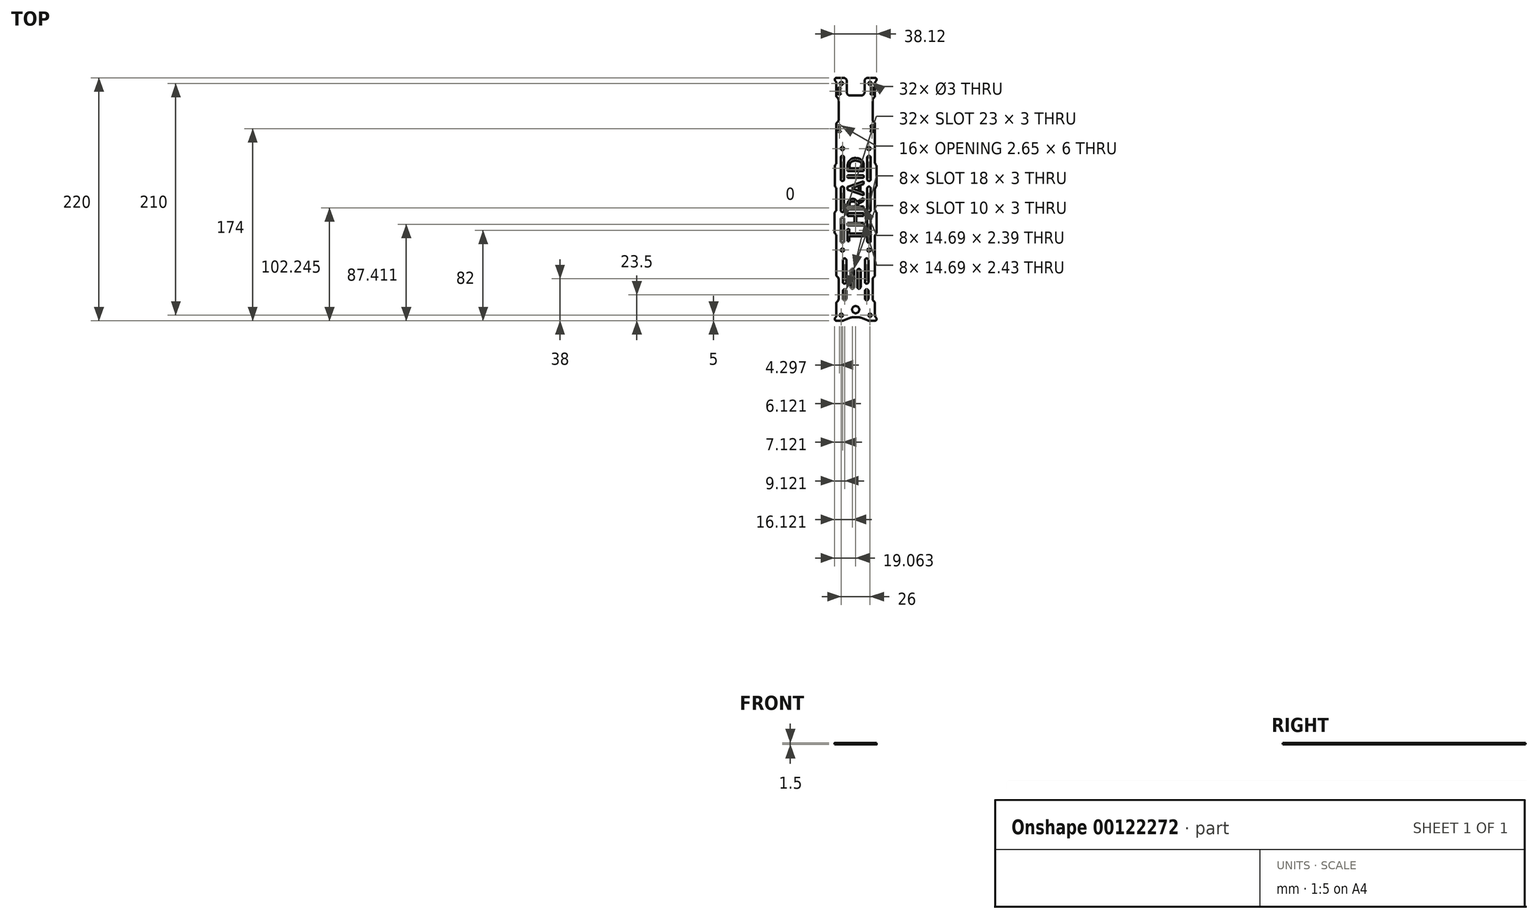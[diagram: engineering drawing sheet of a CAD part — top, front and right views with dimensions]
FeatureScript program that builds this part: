
annotation { "Feature Type Name" : "Feature", "Feature Type Description" : "" }
export const myFeature = defineFeature(function(context is Context, id is Id, definition is map)
    precondition{}
    {
        {
            var Q0;
            Q0=qCreatedBy(makeId("Top.planeOp"),FACE);
            var sketch = newSketch(context, id + "F0", { "sketchPlane" : qUnion([Q0])});
            skArc(sketch, "E0", {"start": v(-17.44, 110) * mm, "mid": v(-18.84, 109.04) * mm, "end": v(-18.44, 107.38) * mm});
            skArc(sketch, "E1", {"start": v(18.56, 107.38) * mm, "mid": v(18.96, 109.04) * mm, "end": v(17.56, 110) * mm});
            skArc(sketch, "E2", {"start": v(-17.44, 105.15) * mm, "mid": v(-17.7, 106.37) * mm, "end": v(-18.44, 107.38) * mm});
            skArc(sketch, "E3", {"start": v(18.56, 107.38) * mm, "mid": v(17.82, 106.37) * mm, "end": v(17.56, 105.15) * mm});
            skLineSegment(sketch, "E4", {"start": v(-17.44, -110) * mm, "end": v(-12.02, -110) * mm});
            skLineSegment(sketch, "E5", {"start": v(12.14, -110) * mm, "end": v(17.56, -110) * mm});
            skArc(sketch, "E6", {"start": v(-18.44, -107.38) * mm, "mid": v(-18.84, -109.04) * mm, "end": v(-17.44, -110) * mm});
            skArc(sketch, "E7", {"start": v(17.56, -110) * mm, "mid": v(18.96, -109.04) * mm, "end": v(18.56, -107.38) * mm});
            skLineSegment(sketch, "E8", {"start": v(11.03, -109.79) * mm, "end": v(4.6, -107.21) * mm});
            skLineSegment(sketch, "E9", {"start": v(-4.47, -107.21) * mm, "end": v(-10.9, -109.79) * mm});
            skArc(sketch, "E10", {"start": v(-18.44, -107.38) * mm, "mid": v(-17.7, -106.37) * mm, "end": v(-17.44, -105.15) * mm});
            skArc(sketch, "E11", {"start": v(-12.02, -110) * mm, "mid": v(-11.45, -109.95) * mm, "end": v(-10.9, -109.79) * mm});
            skArc(sketch, "E12", {"start": v(-3.36, -107) * mm, "mid": v(-3.93, -107.05) * mm, "end": v(-4.47, -107.21) * mm});
            skArc(sketch, "E13", {"start": v(4.6, -107.21) * mm, "mid": v(4.05, -107.05) * mm, "end": v(3.48, -107) * mm});
            skArc(sketch, "E14", {"start": v(11.03, -109.79) * mm, "mid": v(11.57, -109.95) * mm, "end": v(12.14, -110) * mm});
            skArc(sketch, "E15", {"start": v(17.56, -105.15) * mm, "mid": v(17.82, -106.37) * mm, "end": v(18.56, -107.38) * mm});
            skCircle(sketch, "E16", {"center": v(12.06, -46) * mm, "radius": 1.5 * mm});
            skCircle(sketch, "E17", {"center": v(-11.94, -46) * mm, "radius": 1.5 * mm});
            skLineSegment(sketch, "E18", {"start": v(15.56, 77.5) * mm, "end": v(15.56, 84.5) * mm});
            skLineSegment(sketch, "E19", {"start": v(-15.44, 84.5) * mm, "end": v(-15.44, 77.5) * mm});
            skLineSegment(sketch, "E20", {"start": v(15.56, 90.17) * mm, "end": v(15.56, 71.83) * mm});
            skLineSegment(sketch, "E21", {"start": v(17.56, 105.15) * mm, "end": v(17.56, 93.83) * mm});
            skLineSegment(sketch, "E22", {"start": v(17.56, 68.17) * mm, "end": v(17.56, 45.82) * mm});
            skLineSegment(sketch, "E23", {"start": v(16.15, 91.59) * mm, "end": v(16.98, 92.41) * mm});
            skLineSegment(sketch, "E24", {"start": v(16.98, 69.59) * mm, "end": v(16.15, 70.41) * mm});
            skLineSegment(sketch, "E25", {"start": v(-15.44, 71.83) * mm, "end": v(-15.44, 90.17) * mm});
            skLineSegment(sketch, "E26", {"start": v(-16.02, 91.59) * mm, "end": v(-16.85, 92.41) * mm});
            skLineSegment(sketch, "E27", {"start": v(-16.85, 69.59) * mm, "end": v(-16.02, 70.41) * mm});
            skLineSegment(sketch, "E28", {"start": v(-17.44, 105.15) * mm, "end": v(-17.44, 93.83) * mm});
            skLineSegment(sketch, "E29", {"start": v(-17.44, 45.82) * mm, "end": v(-17.44, 68.17) * mm});
            skArc(sketch, "E30", {"start": v(-17.44, 93.83) * mm, "mid": v(-17.29, 93.06) * mm, "end": v(-16.85, 92.41) * mm});
            skArc(sketch, "E31", {"start": v(-15.44, 90.17) * mm, "mid": v(-15.6, 90.94) * mm, "end": v(-16.02, 91.59) * mm});
            skArc(sketch, "E32", {"start": v(-16.85, 69.59) * mm, "mid": v(-17.29, 68.94) * mm, "end": v(-17.44, 68.17) * mm});
            skArc(sketch, "E33", {"start": v(-16.02, 70.41) * mm, "mid": v(-15.6, 71.06) * mm, "end": v(-15.44, 71.83) * mm});
            skArc(sketch, "E34", {"start": v(16.98, 92.41) * mm, "mid": v(17.4, 93.06) * mm, "end": v(17.56, 93.83) * mm});
            skArc(sketch, "E35", {"start": v(16.15, 91.59) * mm, "mid": v(15.71, 90.94) * mm, "end": v(15.56, 90.17) * mm});
            skArc(sketch, "E36", {"start": v(15.56, 71.83) * mm, "mid": v(15.71, 71.06) * mm, "end": v(16.15, 70.41) * mm});
            skArc(sketch, "E37", {"start": v(17.56, 68.17) * mm, "mid": v(17.4, 68.94) * mm, "end": v(16.98, 69.59) * mm});
            skLineSegment(sketch, "E38", {"start": v(15.56, -91.32) * mm, "end": v(15.56, -72.15) * mm});
            skLineSegment(sketch, "E39", {"start": v(-17.44, -45.82) * mm, "end": v(-17.44, -68.49) * mm});
            skLineSegment(sketch, "E40", {"start": v(17.56, -68.49) * mm, "end": v(17.56, -45.82) * mm});
            skLineSegment(sketch, "E41", {"start": v(16.98, -69.9) * mm, "end": v(16.15, -70.73) * mm});
            skLineSegment(sketch, "E42", {"start": v(-16.02, -70.73) * mm, "end": v(-16.85, -69.9) * mm});
            skLineSegment(sketch, "E43", {"start": v(17.56, -93.32) * mm, "end": v(15.56, -91.32) * mm});
            skLineSegment(sketch, "E44", {"start": v(-16.85, -92.73) * mm, "end": v(-16.02, -91.9) * mm});
            skLineSegment(sketch, "E45", {"start": v(-17.44, -94.15) * mm, "end": v(-17.44, -105.15) * mm});
            skLineSegment(sketch, "E46", {"start": v(17.56, -105.15) * mm, "end": v(17.56, -93.32) * mm});
            skLineSegment(sketch, "E47", {"start": v(-15.44, -72.15) * mm, "end": v(-15.44, -90.49) * mm});
            skArc(sketch, "E48", {"start": v(-16.85, -92.73) * mm, "mid": v(-17.29, -93.38) * mm, "end": v(-17.44, -94.15) * mm});
            skArc(sketch, "E49", {"start": v(-16.02, -91.9) * mm, "mid": v(-15.6, -91.25) * mm, "end": v(-15.44, -90.49) * mm});
            skArc(sketch, "E50", {"start": v(-17.44, -68.49) * mm, "mid": v(-17.29, -69.25) * mm, "end": v(-16.85, -69.9) * mm});
            skArc(sketch, "E51", {"start": v(-15.44, -72.15) * mm, "mid": v(-15.6, -71.38) * mm, "end": v(-16.02, -70.73) * mm});
            skArc(sketch, "E52", {"start": v(16.15, -70.73) * mm, "mid": v(15.71, -71.38) * mm, "end": v(15.56, -72.15) * mm});
            skArc(sketch, "E53", {"start": v(16.98, -69.9) * mm, "mid": v(17.4, -69.25) * mm, "end": v(17.56, -68.49) * mm});
            skCircle(sketch, "E54", {"center": v(-11.94, 46) * mm, "radius": 1.5 * mm});
            skCircle(sketch, "E55", {"center": v(12.06, 46) * mm, "radius": 1.5 * mm});
            skLineSegment(sketch, "E56", {"start": v(3.48, -107) * mm, "end": v(-3.36, -107) * mm});
            skLineSegment(sketch, "E57", {"start": v(17.56, -9.4) * mm, "end": v(17.56, 9.33) * mm});
            skLineSegment(sketch, "E58", {"start": v(-17.44, 9.33) * mm, "end": v(-17.44, -9.3) * mm});
            skLineSegment(sketch, "E59", {"start": v(17.56, 45.82) * mm, "end": v(17.56, 33.17) * mm});
            skLineSegment(sketch, "E60", {"start": v(17.56, -33.14) * mm, "end": v(17.56, -45.82) * mm});
            skLineSegment(sketch, "E61", {"start": v(-17.44, -45.82) * mm, "end": v(-17.44, -33.23) * mm});
            skLineSegment(sketch, "E62", {"start": v(-17.44, 33.17) * mm, "end": v(-17.44, 45.82) * mm});
            skLineSegment(sketch, "E63", {"start": v(19.06, 12.67) * mm, "end": v(19.06, 29.83) * mm});
            skLineSegment(sketch, "E64", {"start": v(-18.94, 29.83) * mm, "end": v(-18.94, 12.67) * mm});
            skLineSegment(sketch, "E65", {"start": v(18.94, -29.92) * mm, "end": v(18.94, -12.66) * mm});
            skLineSegment(sketch, "E66", {"start": v(-19.06, -12.75) * mm, "end": v(-19.06, -29.83) * mm});
            skLineSegment(sketch, "E67", {"start": v(-17.9, -31.94) * mm, "end": v(-18.6, -31.11) * mm});
            skLineSegment(sketch, "E68", {"start": v(17.93, -31.98) * mm, "end": v(18.57, -31.08) * mm});
            skLineSegment(sketch, "E69", {"start": v(18.6, -11.55) * mm, "end": v(17.9, -10.5) * mm});
            skLineSegment(sketch, "E70", {"start": v(-18.63, -11.51) * mm, "end": v(-17.87, -10.54) * mm});
            skLineSegment(sketch, "E71", {"start": v(17.96, 10.53) * mm, "end": v(18.66, 11.47) * mm});
            skLineSegment(sketch, "E72", {"start": v(-17.84, 10.53) * mm, "end": v(-18.54, 11.47) * mm});
            skLineSegment(sketch, "E73", {"start": v(-18.54, 31.03) * mm, "end": v(-17.84, 31.97) * mm});
            skLineSegment(sketch, "E74", {"start": v(17.96, 31.97) * mm, "end": v(18.66, 31.03) * mm});
            skArc(sketch, "E75", {"start": v(-17.84, 31.97) * mm, "mid": v(-17.54, 32.53) * mm, "end": v(-17.44, 33.17) * mm});
            skArc(sketch, "E76", {"start": v(-18.54, 31.03) * mm, "mid": v(-18.84, 30.47) * mm, "end": v(-18.94, 29.83) * mm});
            skArc(sketch, "E77", {"start": v(-18.94, 12.67) * mm, "mid": v(-18.84, 12.03) * mm, "end": v(-18.54, 11.47) * mm});
            skArc(sketch, "E78", {"start": v(-17.44, 9.33) * mm, "mid": v(-17.54, 9.97) * mm, "end": v(-17.84, 10.53) * mm});
            skArc(sketch, "E79", {"start": v(17.56, 33.17) * mm, "mid": v(17.66, 32.53) * mm, "end": v(17.96, 31.97) * mm});
            skArc(sketch, "E80", {"start": v(19.06, 29.83) * mm, "mid": v(18.96, 30.47) * mm, "end": v(18.66, 31.03) * mm});
            skArc(sketch, "E81", {"start": v(18.66, 11.47) * mm, "mid": v(18.96, 12.03) * mm, "end": v(19.06, 12.67) * mm});
            skArc(sketch, "E82", {"start": v(17.96, 10.53) * mm, "mid": v(17.66, 9.97) * mm, "end": v(17.56, 9.33) * mm});
            skArc(sketch, "E83", {"start": v(17.56, -9.4) * mm, "mid": v(17.65, -9.97) * mm, "end": v(17.9, -10.5) * mm});
            skArc(sketch, "E84", {"start": v(18.94, -12.66) * mm, "mid": v(18.85, -12.08) * mm, "end": v(18.6, -11.55) * mm});
            skArc(sketch, "E85", {"start": v(-17.87, -10.54) * mm, "mid": v(-17.55, -9.96) * mm, "end": v(-17.44, -9.3) * mm});
            skArc(sketch, "E86", {"start": v(-18.63, -11.51) * mm, "mid": v(-18.95, -12.1) * mm, "end": v(-19.06, -12.75) * mm});
            skArc(sketch, "E87", {"start": v(18.57, -31.08) * mm, "mid": v(18.84, -30.53) * mm, "end": v(18.94, -29.92) * mm});
            skArc(sketch, "E88", {"start": v(17.93, -31.98) * mm, "mid": v(17.66, -32.53) * mm, "end": v(17.56, -33.14) * mm});
            skArc(sketch, "E89", {"start": v(-17.44, -33.23) * mm, "mid": v(-17.56, -32.54) * mm, "end": v(-17.9, -31.94) * mm});
            skArc(sketch, "E90", {"start": v(-19.06, -29.83) * mm, "mid": v(-18.94, -30.51) * mm, "end": v(-18.6, -31.11) * mm});
            skLineSegment(sketch, "E91", {"start": v(13.56, -10) * mm, "end": v(13.56, 10) * mm});
            skLineSegment(sketch, "E92", {"start": v(10.56, 10) * mm, "end": v(10.56, -10) * mm});
            skArc(sketch, "E93", {"start": v(13.56, 10) * mm, "mid": v(12.06, 11.5) * mm, "end": v(10.56, 10) * mm});
            skArc(sketch, "E94", {"start": v(10.56, -10) * mm, "mid": v(12.06, -11.5) * mm, "end": v(13.56, -10) * mm});
            skLineSegment(sketch, "E95", {"start": v(-10.44, -10) * mm, "end": v(-10.44, 10) * mm});
            skLineSegment(sketch, "E96", {"start": v(-13.44, 10) * mm, "end": v(-13.44, -10) * mm});
            skArc(sketch, "E97", {"start": v(-10.44, 10) * mm, "mid": v(-11.94, 11.5) * mm, "end": v(-13.44, 10) * mm});
            skArc(sketch, "E98", {"start": v(-13.44, -10) * mm, "mid": v(-11.94, -11.5) * mm, "end": v(-10.44, -10) * mm});
            skLineSegment(sketch, "E99", {"start": v(13.56, 18) * mm, "end": v(13.56, 38) * mm});
            skLineSegment(sketch, "E100", {"start": v(10.56, 38) * mm, "end": v(10.56, 18) * mm});
            skArc(sketch, "E101", {"start": v(13.56, 38) * mm, "mid": v(12.06, 39.5) * mm, "end": v(10.56, 38) * mm});
            skArc(sketch, "E102", {"start": v(10.56, 18) * mm, "mid": v(12.06, 16.5) * mm, "end": v(13.56, 18) * mm});
            skLineSegment(sketch, "E103", {"start": v(-10.44, 18) * mm, "end": v(-10.44, 38) * mm});
            skLineSegment(sketch, "E104", {"start": v(-13.44, 38) * mm, "end": v(-13.44, 18) * mm});
            skArc(sketch, "E105", {"start": v(-10.44, 38) * mm, "mid": v(-11.94, 39.5) * mm, "end": v(-13.44, 38) * mm});
            skArc(sketch, "E106", {"start": v(-13.44, 18) * mm, "mid": v(-11.94, 16.5) * mm, "end": v(-10.44, 18) * mm});
            skLineSegment(sketch, "E107", {"start": v(13.56, -38) * mm, "end": v(13.56, -18) * mm});
            skLineSegment(sketch, "E108", {"start": v(10.56, -18) * mm, "end": v(10.56, -38) * mm});
            skArc(sketch, "E109", {"start": v(13.56, -18) * mm, "mid": v(12.06, -16.5) * mm, "end": v(10.56, -18) * mm});
            skArc(sketch, "E110", {"start": v(10.56, -38) * mm, "mid": v(12.06, -39.5) * mm, "end": v(13.56, -38) * mm});
            skLineSegment(sketch, "E111", {"start": v(-10.44, -38) * mm, "end": v(-10.44, -18) * mm});
            skLineSegment(sketch, "E112", {"start": v(-13.44, -18) * mm, "end": v(-13.44, -38) * mm});
            skArc(sketch, "E113", {"start": v(-10.44, -18) * mm, "mid": v(-11.94, -16.5) * mm, "end": v(-13.44, -18) * mm});
            skArc(sketch, "E114", {"start": v(-13.44, -38) * mm, "mid": v(-11.94, -39.5) * mm, "end": v(-10.44, -38) * mm});
            skLineSegment(sketch, "E115", {"start": v(11.56, -75) * mm, "end": v(11.56, -55) * mm});
            skLineSegment(sketch, "E116", {"start": v(8.56, -55) * mm, "end": v(8.56, -75) * mm});
            skArc(sketch, "E117", {"start": v(11.56, -55) * mm, "mid": v(10.06, -53.5) * mm, "end": v(8.56, -55) * mm});
            skArc(sketch, "E118", {"start": v(8.56, -75) * mm, "mid": v(10.06, -76.5) * mm, "end": v(11.56, -75) * mm});
            skLineSegment(sketch, "E119", {"start": v(-8.44, -75) * mm, "end": v(-8.44, -55) * mm});
            skLineSegment(sketch, "E120", {"start": v(-11.44, -55) * mm, "end": v(-11.44, -75) * mm});
            skArc(sketch, "E121", {"start": v(-8.44, -55) * mm, "mid": v(-9.94, -53.5) * mm, "end": v(-11.44, -55) * mm});
            skArc(sketch, "E122", {"start": v(-11.44, -75) * mm, "mid": v(-9.94, -76.5) * mm, "end": v(-8.44, -75) * mm});
            skLineSegment(sketch, "E123", {"start": v(11.56, -90) * mm, "end": v(11.56, -83) * mm});
            skLineSegment(sketch, "E124", {"start": v(8.56, -83) * mm, "end": v(8.56, -90) * mm});
            skLineSegment(sketch, "E125", {"start": v(-8.44, -90) * mm, "end": v(-8.44, -83) * mm});
            skLineSegment(sketch, "E126", {"start": v(-11.44, -83) * mm, "end": v(-11.44, -90) * mm});
            skArc(sketch, "E127", {"start": v(-8.44, -83) * mm, "mid": v(-9.94, -81.5) * mm, "end": v(-11.44, -83) * mm});
            skArc(sketch, "E128", {"start": v(11.56, -83) * mm, "mid": v(10.06, -81.5) * mm, "end": v(8.56, -83) * mm});
            skLineSegment(sketch, "E129", {"start": v(-13.94, 101) * mm, "end": v(-15.59, 101) * mm});
            skLineSegment(sketch, "E130", {"start": v(-15.59, 61) * mm, "end": v(-13.94, 61) * mm});
            skLineSegment(sketch, "E131", {"start": v(-13.94, 67) * mm, "end": v(-15.59, 67) * mm});
            skLineSegment(sketch, "E132", {"start": v(14.06, 61) * mm, "end": v(15.71, 61) * mm});
            skLineSegment(sketch, "E133", {"start": v(15.71, 67) * mm, "end": v(14.06, 67) * mm});
            skLineSegment(sketch, "E134", {"start": v(15.71, 101) * mm, "end": v(14.06, 101) * mm});
            skLineSegment(sketch, "E135", {"start": v(-15.59, 95) * mm, "end": v(-13.94, 95) * mm});
            skLineSegment(sketch, "E136", {"start": v(14.06, 95) * mm, "end": v(15.71, 95) * mm});
            skArc(sketch, "E137", {"start": v(-15.59, 101) * mm, "mid": v(-16.07, 100.63) * mm, "end": v(-15.84, 100.07) * mm});
            skArc(sketch, "E138", {"start": v(-15.84, 95.93) * mm, "mid": v(-16.07, 95.37) * mm, "end": v(-15.59, 95) * mm});
            skArc(sketch, "E139", {"start": v(-13.94, 95) * mm, "mid": v(-13.46, 95.37) * mm, "end": v(-13.69, 95.93) * mm});
            skArc(sketch, "E140", {"start": v(-13.69, 100.07) * mm, "mid": v(-13.46, 100.63) * mm, "end": v(-13.94, 101) * mm});
            skArc(sketch, "E141", {"start": v(14.06, 101) * mm, "mid": v(13.58, 100.63) * mm, "end": v(13.81, 100.07) * mm});
            skArc(sketch, "E142", {"start": v(13.81, 95.93) * mm, "mid": v(13.58, 95.37) * mm, "end": v(14.06, 95) * mm});
            skArc(sketch, "E143", {"start": v(15.71, 95) * mm, "mid": v(16.2, 95.37) * mm, "end": v(15.96, 95.93) * mm});
            skArc(sketch, "E144", {"start": v(15.96, 100.07) * mm, "mid": v(16.2, 100.63) * mm, "end": v(15.71, 101) * mm});
            skArc(sketch, "E145", {"start": v(14.06, 67) * mm, "mid": v(13.58, 66.63) * mm, "end": v(13.81, 66.07) * mm});
            skArc(sketch, "E146", {"start": v(13.81, 61.93) * mm, "mid": v(13.58, 61.37) * mm, "end": v(14.06, 61) * mm});
            skArc(sketch, "E147", {"start": v(15.71, 61) * mm, "mid": v(16.2, 61.37) * mm, "end": v(15.96, 61.93) * mm});
            skArc(sketch, "E148", {"start": v(15.96, 66.07) * mm, "mid": v(16.2, 66.63) * mm, "end": v(15.71, 67) * mm});
            skArc(sketch, "E149", {"start": v(-13.94, 61) * mm, "mid": v(-13.46, 61.37) * mm, "end": v(-13.69, 61.93) * mm});
            skArc(sketch, "E150", {"start": v(-13.69, 66.07) * mm, "mid": v(-13.46, 66.63) * mm, "end": v(-13.94, 67) * mm});
            skArc(sketch, "E151", {"start": v(-15.59, 67) * mm, "mid": v(-16.07, 66.63) * mm, "end": v(-15.84, 66.07) * mm});
            skArc(sketch, "E152", {"start": v(-15.84, 61.93) * mm, "mid": v(-16.07, 61.37) * mm, "end": v(-15.59, 61) * mm});
            skLineSegment(sketch, "E153", {"start": v(-15.59, 99.63) * mm, "end": v(-15.59, 96.37) * mm});
            skLineSegment(sketch, "E154", {"start": v(-13.94, 96.37) * mm, "end": v(-13.94, 99.63) * mm});
            skLineSegment(sketch, "E155", {"start": v(14.06, 99.63) * mm, "end": v(14.06, 96.37) * mm});
            skLineSegment(sketch, "E156", {"start": v(15.71, 96.37) * mm, "end": v(15.71, 99.63) * mm});
            skLineSegment(sketch, "E157", {"start": v(14.06, 65.63) * mm, "end": v(14.06, 62.37) * mm});
            skLineSegment(sketch, "E158", {"start": v(15.71, 62.37) * mm, "end": v(15.71, 65.63) * mm});
            skLineSegment(sketch, "E159", {"start": v(-13.94, 65.63) * mm, "end": v(-13.94, 62.37) * mm});
            skLineSegment(sketch, "E160", {"start": v(-15.59, 62.37) * mm, "end": v(-15.59, 65.63) * mm});
            skArc(sketch, "E161", {"start": v(-15.59, 99.63) * mm, "mid": v(-15.66, 99.88) * mm, "end": v(-15.84, 100.07) * mm});
            skArc(sketch, "E162", {"start": v(-13.69, 100.07) * mm, "mid": v(-13.87, 99.88) * mm, "end": v(-13.94, 99.63) * mm});
            skArc(sketch, "E163", {"start": v(-13.94, 96.37) * mm, "mid": v(-13.87, 96.12) * mm, "end": v(-13.69, 95.93) * mm});
            skArc(sketch, "E164", {"start": v(-15.84, 95.93) * mm, "mid": v(-15.66, 96.12) * mm, "end": v(-15.59, 96.37) * mm});
            skArc(sketch, "E165", {"start": v(14.06, 99.63) * mm, "mid": v(14, 99.88) * mm, "end": v(13.81, 100.07) * mm});
            skArc(sketch, "E166", {"start": v(15.96, 100.07) * mm, "mid": v(15.78, 99.88) * mm, "end": v(15.71, 99.63) * mm});
            skArc(sketch, "E167", {"start": v(15.71, 96.37) * mm, "mid": v(15.78, 96.12) * mm, "end": v(15.96, 95.93) * mm});
            skArc(sketch, "E168", {"start": v(13.81, 95.93) * mm, "mid": v(14, 96.12) * mm, "end": v(14.06, 96.37) * mm});
            skArc(sketch, "E169", {"start": v(14.06, 65.63) * mm, "mid": v(14, 65.88) * mm, "end": v(13.81, 66.07) * mm});
            skArc(sketch, "E170", {"start": v(15.96, 66.07) * mm, "mid": v(15.78, 65.88) * mm, "end": v(15.71, 65.63) * mm});
            skArc(sketch, "E171", {"start": v(15.71, 62.37) * mm, "mid": v(15.78, 62.12) * mm, "end": v(15.96, 61.93) * mm});
            skArc(sketch, "E172", {"start": v(13.81, 61.93) * mm, "mid": v(14, 62.12) * mm, "end": v(14.06, 62.37) * mm});
            skArc(sketch, "E173", {"start": v(-13.94, 62.37) * mm, "mid": v(-13.87, 62.12) * mm, "end": v(-13.69, 61.93) * mm});
            skArc(sketch, "E174", {"start": v(-15.84, 61.93) * mm, "mid": v(-15.66, 62.12) * mm, "end": v(-15.59, 62.37) * mm});
            skArc(sketch, "E175", {"start": v(-15.59, 65.63) * mm, "mid": v(-15.66, 65.88) * mm, "end": v(-15.84, 66.07) * mm});
            skArc(sketch, "E176", {"start": v(-13.69, 66.07) * mm, "mid": v(-13.87, 65.88) * mm, "end": v(-13.94, 65.63) * mm});
            skLineSegment(sketch, "E177", {"start": v(4.56, -79.5) * mm, "end": v(4.56, -64.5) * mm});
            skLineSegment(sketch, "E178", {"start": v(1.56, -64.5) * mm, "end": v(1.56, -79.5) * mm});
            skLineSegment(sketch, "E179", {"start": v(-1.44, -79.5) * mm, "end": v(-1.44, -64.5) * mm});
            skLineSegment(sketch, "E180", {"start": v(-4.44, -64.5) * mm, "end": v(-4.44, -79.5) * mm});
            skArc(sketch, "E181", {"start": v(4.56, -64.5) * mm, "mid": v(3.06, -63) * mm, "end": v(1.56, -64.5) * mm});
            skArc(sketch, "E182", {"start": v(-1.44, -64.5) * mm, "mid": v(-2.94, -63) * mm, "end": v(-4.44, -64.5) * mm});
            skArc(sketch, "E183", {"start": v(-4.44, -79.5) * mm, "mid": v(-2.94, -81) * mm, "end": v(-1.44, -79.5) * mm});
            skArc(sketch, "E184", {"start": v(1.56, -79.5) * mm, "mid": v(3.06, -81) * mm, "end": v(4.56, -79.5) * mm});
            skCircle(sketch, "E185", {"center": v(13.06, 105) * mm, "radius": 1.5 * mm});
            skCircle(sketch, "E186", {"center": v(-12.94, 105) * mm, "radius": 1.5 * mm});
            skCircle(sketch, "E187", {"center": v(13.06, -105) * mm, "radius": 1.5 * mm});
            skCircle(sketch, "E188", {"center": v(-12.94, -105) * mm, "radius": 1.5 * mm});
            skLineSegment(sketch, "E189", {"start": v(-4.94, 94) * mm, "end": v(5.06, 94) * mm});
            skLineSegment(sketch, "E190", {"start": v(8.06, 97) * mm, "end": v(8.06, 107) * mm});
            skLineSegment(sketch, "E191", {"start": v(-7.94, 107) * mm, "end": v(-7.94, 97) * mm});
            skLineSegment(sketch, "E192", {"start": v(-17.44, 110) * mm, "end": v(-10.94, 110) * mm});
            skLineSegment(sketch, "E193", {"start": v(11.06, 110) * mm, "end": v(17.56, 110) * mm});
            skArc(sketch, "E194", {"start": v(-7.94, 107) * mm, "mid": v(-8.82, 109.12) * mm, "end": v(-10.94, 110) * mm});
            skArc(sketch, "E195", {"start": v(11.06, 110) * mm, "mid": v(8.94, 109.12) * mm, "end": v(8.06, 107) * mm});
            skArc(sketch, "E196", {"start": v(5.06, 94) * mm, "mid": v(7.18, 94.88) * mm, "end": v(8.06, 97) * mm});
            skArc(sketch, "E197", {"start": v(-7.94, 97) * mm, "mid": v(-7.06, 94.88) * mm, "end": v(-4.94, 94) * mm});
            skArc(sketch, "E198", {"start": v(-11.44, -90) * mm, "mid": v(-9.94, -91.5) * mm, "end": v(-8.44, -90) * mm});
            skArc(sketch, "E199", {"start": v(8.56, -90) * mm, "mid": v(10.06, -91.5) * mm, "end": v(11.56, -90) * mm});
            skCircle(sketch, "E200", {"center": v(0.06, -100) * mm, "radius": 3.25 * mm});
            skSolve(sketch);
        }
        {
            var Q0;
            Q0=makeQuery(id+"F0.imprint","IMPRINT",FACE,{"disambiguationData":[TD([[makeQuery(id+"F0.imprint","IMPRINT",EDGE,{"derivedFrom":sQuery(id+"F0.wireOp",EDGE,"E0")}),1.0]])]});
            extrude(context, id + "F1", {"entities" : qUnion([Q0]), "depth" : 1.5 * mm});
        }
        {
            var Q0;
            Q0=makeQuery(id+"F1.opExtrude","CAP_FACE",FACE,{"disambiguationData":[OSD([sQuery(id+"F0.wireOp",EDGE,"E0"),sQuery(id+"F0.wireOp",EDGE,"E1"),sQuery(id+"F0.wireOp",EDGE,"E2"),sQuery(id+"F0.wireOp",EDGE,"E3"),sQuery(id+"F0.wireOp",EDGE,"E4"),sQuery(id+"F0.wireOp",EDGE,"E5"),sQuery(id+"F0.wireOp",EDGE,"E6"),sQuery(id+"F0.wireOp",EDGE,"E7"),sQuery(id+"F0.wireOp",EDGE,"E8"),sQuery(id+"F0.wireOp",EDGE,"E9"),sQuery(id+"F0.wireOp",EDGE,"E10"),sQuery(id+"F0.wireOp",EDGE,"E11"),sQuery(id+"F0.wireOp",EDGE,"E12"),sQuery(id+"F0.wireOp",EDGE,"E13"),sQuery(id+"F0.wireOp",EDGE,"E14"),sQuery(id+"F0.wireOp",EDGE,"E15"),sQuery(id+"F0.wireOp",EDGE,"E16"),sQuery(id+"F0.wireOp",EDGE,"E17"),sQuery(id+"F0.wireOp",EDGE,"E20"),sQuery(id+"F0.wireOp",EDGE,"E21"),sQuery(id+"F0.wireOp",EDGE,"E22"),sQuery(id+"F0.wireOp",EDGE,"E23"),sQuery(id+"F0.wireOp",EDGE,"E24"),sQuery(id+"F0.wireOp",EDGE,"E25"),sQuery(id+"F0.wireOp",EDGE,"E26"),sQuery(id+"F0.wireOp",EDGE,"E27"),sQuery(id+"F0.wireOp",EDGE,"E28"),sQuery(id+"F0.wireOp",EDGE,"E29"),sQuery(id+"F0.wireOp",EDGE,"E30"),sQuery(id+"F0.wireOp",EDGE,"E31"),sQuery(id+"F0.wireOp",EDGE,"E32"),sQuery(id+"F0.wireOp",EDGE,"E33"),sQuery(id+"F0.wireOp",EDGE,"E34"),sQuery(id+"F0.wireOp",EDGE,"E35"),sQuery(id+"F0.wireOp",EDGE,"E36"),sQuery(id+"F0.wireOp",EDGE,"E37"),sQuery(id+"F0.wireOp",EDGE,"E38"),sQuery(id+"F0.wireOp",EDGE,"E39"),sQuery(id+"F0.wireOp",EDGE,"E40"),sQuery(id+"F0.wireOp",EDGE,"E41"),sQuery(id+"F0.wireOp",EDGE,"E42"),sQuery(id+"F0.wireOp",EDGE,"E43"),sQuery(id+"F0.wireOp",EDGE,"E44"),sQuery(id+"F0.wireOp",EDGE,"E45"),sQuery(id+"F0.wireOp",EDGE,"E46"),sQuery(id+"F0.wireOp",EDGE,"E47"),sQuery(id+"F0.wireOp",EDGE,"E48"),sQuery(id+"F0.wireOp",EDGE,"E49"),sQuery(id+"F0.wireOp",EDGE,"E50"),sQuery(id+"F0.wireOp",EDGE,"E51"),sQuery(id+"F0.wireOp",EDGE,"E52"),sQuery(id+"F0.wireOp",EDGE,"E53"),sQuery(id+"F0.wireOp",EDGE,"E54"),sQuery(id+"F0.wireOp",EDGE,"E55"),sQuery(id+"F0.wireOp",EDGE,"E56"),sQuery(id+"F0.wireOp",EDGE,"E57"),sQuery(id+"F0.wireOp",EDGE,"E58"),sQuery(id+"F0.wireOp",EDGE,"E59"),sQuery(id+"F0.wireOp",EDGE,"E60"),sQuery(id+"F0.wireOp",EDGE,"E61"),sQuery(id+"F0.wireOp",EDGE,"E62"),sQuery(id+"F0.wireOp",EDGE,"E63"),sQuery(id+"F0.wireOp",EDGE,"E64"),sQuery(id+"F0.wireOp",EDGE,"E65"),sQuery(id+"F0.wireOp",EDGE,"E66"),sQuery(id+"F0.wireOp",EDGE,"E67"),sQuery(id+"F0.wireOp",EDGE,"E68"),sQuery(id+"F0.wireOp",EDGE,"E69"),sQuery(id+"F0.wireOp",EDGE,"E70"),sQuery(id+"F0.wireOp",EDGE,"E71"),sQuery(id+"F0.wireOp",EDGE,"E72"),sQuery(id+"F0.wireOp",EDGE,"E73"),sQuery(id+"F0.wireOp",EDGE,"E74"),sQuery(id+"F0.wireOp",EDGE,"E75"),sQuery(id+"F0.wireOp",EDGE,"E76"),sQuery(id+"F0.wireOp",EDGE,"E77"),sQuery(id+"F0.wireOp",EDGE,"E78"),sQuery(id+"F0.wireOp",EDGE,"E79"),sQuery(id+"F0.wireOp",EDGE,"E80"),sQuery(id+"F0.wireOp",EDGE,"E81"),sQuery(id+"F0.wireOp",EDGE,"E82"),sQuery(id+"F0.wireOp",EDGE,"E83"),sQuery(id+"F0.wireOp",EDGE,"E84"),sQuery(id+"F0.wireOp",EDGE,"E85"),sQuery(id+"F0.wireOp",EDGE,"E86"),sQuery(id+"F0.wireOp",EDGE,"E87"),sQuery(id+"F0.wireOp",EDGE,"E88"),sQuery(id+"F0.wireOp",EDGE,"E89"),sQuery(id+"F0.wireOp",EDGE,"E90"),sQuery(id+"F0.wireOp",EDGE,"E91"),sQuery(id+"F0.wireOp",EDGE,"E92"),sQuery(id+"F0.wireOp",EDGE,"E93"),sQuery(id+"F0.wireOp",EDGE,"E94"),sQuery(id+"F0.wireOp",EDGE,"E95"),sQuery(id+"F0.wireOp",EDGE,"E96"),sQuery(id+"F0.wireOp",EDGE,"E97"),sQuery(id+"F0.wireOp",EDGE,"E98"),sQuery(id+"F0.wireOp",EDGE,"E99"),sQuery(id+"F0.wireOp",EDGE,"E100"),sQuery(id+"F0.wireOp",EDGE,"E101"),sQuery(id+"F0.wireOp",EDGE,"E102"),sQuery(id+"F0.wireOp",EDGE,"E103"),sQuery(id+"F0.wireOp",EDGE,"E104"),sQuery(id+"F0.wireOp",EDGE,"E105"),sQuery(id+"F0.wireOp",EDGE,"E106"),sQuery(id+"F0.wireOp",EDGE,"E107"),sQuery(id+"F0.wireOp",EDGE,"E108"),sQuery(id+"F0.wireOp",EDGE,"E109"),sQuery(id+"F0.wireOp",EDGE,"E110"),sQuery(id+"F0.wireOp",EDGE,"E111"),sQuery(id+"F0.wireOp",EDGE,"E112"),sQuery(id+"F0.wireOp",EDGE,"E113"),sQuery(id+"F0.wireOp",EDGE,"E114"),sQuery(id+"F0.wireOp",EDGE,"E115"),sQuery(id+"F0.wireOp",EDGE,"E116"),sQuery(id+"F0.wireOp",EDGE,"E117"),sQuery(id+"F0.wireOp",EDGE,"E118"),sQuery(id+"F0.wireOp",EDGE,"E119"),sQuery(id+"F0.wireOp",EDGE,"E120"),sQuery(id+"F0.wireOp",EDGE,"E121"),sQuery(id+"F0.wireOp",EDGE,"E122"),sQuery(id+"F0.wireOp",EDGE,"E123"),sQuery(id+"F0.wireOp",EDGE,"E124"),sQuery(id+"F0.wireOp",EDGE,"E125"),sQuery(id+"F0.wireOp",EDGE,"E126"),sQuery(id+"F0.wireOp",EDGE,"E127"),sQuery(id+"F0.wireOp",EDGE,"E128"),sQuery(id+"F0.wireOp",EDGE,"E129"),sQuery(id+"F0.wireOp",EDGE,"E130"),sQuery(id+"F0.wireOp",EDGE,"E131"),sQuery(id+"F0.wireOp",EDGE,"E132"),sQuery(id+"F0.wireOp",EDGE,"E133"),sQuery(id+"F0.wireOp",EDGE,"E134"),sQuery(id+"F0.wireOp",EDGE,"E135"),sQuery(id+"F0.wireOp",EDGE,"E136"),sQuery(id+"F0.wireOp",EDGE,"E137"),sQuery(id+"F0.wireOp",EDGE,"E138"),sQuery(id+"F0.wireOp",EDGE,"E139"),sQuery(id+"F0.wireOp",EDGE,"E140"),sQuery(id+"F0.wireOp",EDGE,"E141"),sQuery(id+"F0.wireOp",EDGE,"E142"),sQuery(id+"F0.wireOp",EDGE,"E143"),sQuery(id+"F0.wireOp",EDGE,"E144"),sQuery(id+"F0.wireOp",EDGE,"E145"),sQuery(id+"F0.wireOp",EDGE,"E146"),sQuery(id+"F0.wireOp",EDGE,"E147"),sQuery(id+"F0.wireOp",EDGE,"E148"),sQuery(id+"F0.wireOp",EDGE,"E149"),sQuery(id+"F0.wireOp",EDGE,"E150"),sQuery(id+"F0.wireOp",EDGE,"E151"),sQuery(id+"F0.wireOp",EDGE,"E152"),sQuery(id+"F0.wireOp",EDGE,"E153"),sQuery(id+"F0.wireOp",EDGE,"E154"),sQuery(id+"F0.wireOp",EDGE,"E155"),sQuery(id+"F0.wireOp",EDGE,"E156"),sQuery(id+"F0.wireOp",EDGE,"E157"),sQuery(id+"F0.wireOp",EDGE,"E158"),sQuery(id+"F0.wireOp",EDGE,"E159"),sQuery(id+"F0.wireOp",EDGE,"E160"),sQuery(id+"F0.wireOp",EDGE,"E161"),sQuery(id+"F0.wireOp",EDGE,"E162"),sQuery(id+"F0.wireOp",EDGE,"E163"),sQuery(id+"F0.wireOp",EDGE,"E164"),sQuery(id+"F0.wireOp",EDGE,"E165"),sQuery(id+"F0.wireOp",EDGE,"E166"),sQuery(id+"F0.wireOp",EDGE,"E167"),sQuery(id+"F0.wireOp",EDGE,"E168"),sQuery(id+"F0.wireOp",EDGE,"E169"),sQuery(id+"F0.wireOp",EDGE,"E170"),sQuery(id+"F0.wireOp",EDGE,"E171"),sQuery(id+"F0.wireOp",EDGE,"E172"),sQuery(id+"F0.wireOp",EDGE,"E173"),sQuery(id+"F0.wireOp",EDGE,"E174"),sQuery(id+"F0.wireOp",EDGE,"E175"),sQuery(id+"F0.wireOp",EDGE,"E176"),sQuery(id+"F0.wireOp",EDGE,"E177"),sQuery(id+"F0.wireOp",EDGE,"E178"),sQuery(id+"F0.wireOp",EDGE,"E179"),sQuery(id+"F0.wireOp",EDGE,"E180"),sQuery(id+"F0.wireOp",EDGE,"E181"),sQuery(id+"F0.wireOp",EDGE,"E182"),sQuery(id+"F0.wireOp",EDGE,"E183"),sQuery(id+"F0.wireOp",EDGE,"E184"),sQuery(id+"F0.wireOp",EDGE,"E185"),sQuery(id+"F0.wireOp",EDGE,"E186"),sQuery(id+"F0.wireOp",EDGE,"c73ca5a2-442d-4a15-9d25-908f51496d8d"),sQuery(id+"F0.wireOp",EDGE,"E187"),sQuery(id+"F0.wireOp",EDGE,"E188"),sQuery(id+"F0.wireOp",EDGE,"E189"),sQuery(id+"F0.wireOp",EDGE,"E190"),sQuery(id+"F0.wireOp",EDGE,"E191"),sQuery(id+"F0.wireOp",EDGE,"E192"),sQuery(id+"F0.wireOp",EDGE,"E193"),sQuery(id+"F0.wireOp",EDGE,"E194"),sQuery(id+"F0.wireOp",EDGE,"E195"),sQuery(id+"F0.wireOp",EDGE,"E196"),sQuery(id+"F0.wireOp",EDGE,"E197"),sQuery(id+"F0.wireOp",EDGE,"0c973af8-d3dc-4b8a-a66e-5da212425358"),sQuery(id+"F0.wireOp",EDGE,"4fe4ddcf-5b55-4034-b81d-017bfca3a58a"),sQuery(id+"F0.wireOp",EDGE,"88736f7d-f410-48d5-8155-ccca867d64b3"),sQuery(id+"F0.wireOp",EDGE,"6a497504-6ec9-49d0-9bed-219f6b21fc9c"),sQuery(id+"F0.wireOp",EDGE,"c8c6e88b-7eb7-4560-b0a5-3d3921e132f2"),sQuery(id+"F0.wireOp",EDGE,"26b159f5-77e5-4e08-a8e1-3c5908efa760"),sQuery(id+"F0.wireOp",EDGE,"20c17bd7-cea7-4f27-b6d8-6ac0558d4713"),sQuery(id+"F0.wireOp",EDGE,"dd1a023c-ba02-48f6-b77e-d22354fd16ed"),sQuery(id+"F0.wireOp",EDGE,"5cd8de6d-985d-442f-8c5d-4d71a0f364de"),sQuery(id+"F0.wireOp",EDGE,"e91b8da9-fdf2-4894-b288-06284c2eb881"),sQuery(id+"F0.wireOp",EDGE,"4fd15355-90f9-488b-b7e5-88dc0d7d7e4e"),sQuery(id+"F0.wireOp",EDGE,"ea105d2c-8f4c-44fd-a3e0-0a8c5cbdea26"),sQuery(id+"F0.wireOp",EDGE,"4e1b5670-c132-469b-93ed-792898b09b02"),sQuery(id+"F0.wireOp",EDGE,"8c72a3cc-1d7e-478c-ad6b-bd9df661be2b"),sQuery(id+"F0.wireOp",EDGE,"a334ad65-e2fa-48d3-8169-06147bc842f5"),sQuery(id+"F0.wireOp",EDGE,"8142a4a4-74a7-4fd8-a2f7-ff8e5076d5df"),sQuery(id+"F0.wireOp",EDGE,"af7de8ac-355b-41bb-b1bf-cb23c12d0367"),sQuery(id+"F0.wireOp",EDGE,"97aed40c-4629-4054-89fb-46e692c3d2d7"),sQuery(id+"F0.wireOp",EDGE,"1ab8cf87-c714-4295-b0dd-7b46c5fba432"),sQuery(id+"F0.wireOp",EDGE,"59b29172-e8c8-46ae-92b4-8a237019e383"),sQuery(id+"F0.wireOp",EDGE,"fe8499e1-1efc-41c1-aaa1-ed7456406679"),sQuery(id+"F0.wireOp",EDGE,"5a4abddc-34a7-439a-8ec9-ce65ec1ac80b"),sQuery(id+"F0.wireOp",EDGE,"eb1d14ab-30da-483e-90be-1fafc5f09e45"),sQuery(id+"F0.wireOp",EDGE,"30f299a9-4c11-4654-b0a9-ca536e4833e6"),sQuery(id+"F0.wireOp",EDGE,"0e527c34-1209-4d01-b66c-50ac0afde651"),sQuery(id+"F0.wireOp",EDGE,"4695423c-1885-4930-8ef6-59749c6b001c"),sQuery(id+"F0.wireOp",EDGE,"40228b54-18ad-46b7-beb7-f829c680c657"),sQuery(id+"F0.wireOp",EDGE,"0d793964-0798-46ec-bcb8-efb0f65125af"),sQuery(id+"F0.wireOp",EDGE,"8332b839-3da5-4ab9-b798-f6219fbf58bc"),sQuery(id+"F0.wireOp",EDGE,"599acbdf-f09c-4eac-a714-b120e744e201"),sQuery(id+"F0.wireOp",EDGE,"5904b0ce-8ced-4318-b0c3-d88eca3f4054"),sQuery(id+"F0.wireOp",EDGE,"5eb64336-0cb6-48b5-81b1-0add6c425463"),sQuery(id+"F0.wireOp",EDGE,"325b8b41-8ec9-434c-b707-16f56a97f428"),sQuery(id+"F0.wireOp",EDGE,"ca1cebf9-d3ea-4fd0-8c91-4b62e735cd36"),sQuery(id+"F0.wireOp",EDGE,"ea0143fe-5b9d-427d-a034-73a701c1f0c2"),sQuery(id+"F0.wireOp",EDGE,"944bbd91-aea2-4bc3-b8e2-a12e9427e78c"),sQuery(id+"F0.wireOp",EDGE,"219f3728-4336-4cc7-85d2-798a77ca3051"),sQuery(id+"F0.wireOp",EDGE,"52a68ef9-69e9-46b3-b357-e696114e0cf5"),sQuery(id+"F0.wireOp",EDGE,"8e7db2cb-4cb0-4cd2-a60e-af8b71200749"),sQuery(id+"F0.wireOp",EDGE,"c9734b3b-d6a6-42b1-a66b-14e6a2af1ab8"),sQuery(id+"F0.wireOp",EDGE,"ec7ee0d9-4a57-41e3-9b1d-32b3f1f208b0"),sQuery(id+"F0.wireOp",EDGE,"0917d198-c2cc-49ca-a61f-f05b5bad831b"),sQuery(id+"F0.wireOp",EDGE,"67976b40-1ad9-4d47-bde4-4e16af6b61b3"),sQuery(id+"F0.wireOp",EDGE,"E198"),sQuery(id+"F0.wireOp",EDGE,"E199")])],"isStart":false});
            var sketch = newSketch(context, id + "F2", { "sketchPlane" : qUnion([Q0])});
            skText(sketch, "E201", { "text": "THRAID", "fontName": "AllertaStencil-Regular.ttf"});
            const initialGuessF2  = {"E201": [0.00735, -0.0389, 0, 1, 0.0147]};
            skSetInitialGuess(sketch, initialGuessF2);
            skSolve(sketch);
        }
        {
            var Q0;
            Q0=qSketchRegion(id+"F2",true);
            extrude(context, id + "F3", {"entities" : qUnion([Q0]), "operationType" : NewBodyOperationType.REMOVE, "oppositeDirection" : true, "depth" : 25 * mm});
        }
    });
